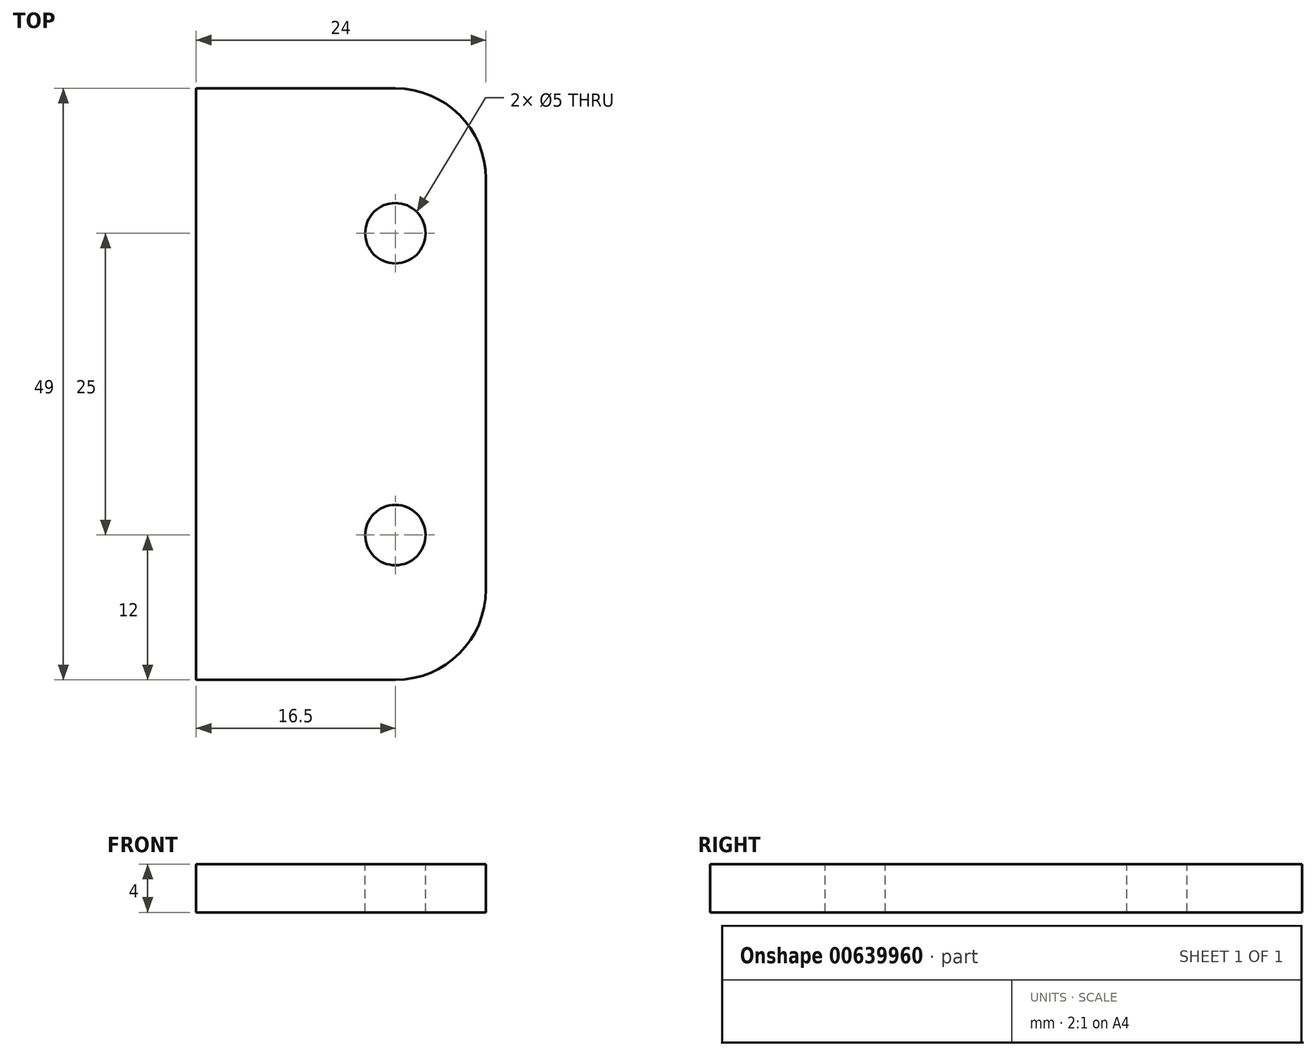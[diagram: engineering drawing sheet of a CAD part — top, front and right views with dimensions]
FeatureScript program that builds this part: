
annotation { "Feature Type Name" : "Feature", "Feature Type Description" : "" }
export const myFeature = defineFeature(function(context is Context, id is Id, definition is map)
    precondition{}
    {
        {
            var Q0;
            Q0=qCreatedBy(makeId("Top.planeOp"),FACE);
            var sketch = newSketch(context, id + "F0", { "sketchPlane" : qUnion([Q0])});
            skLineSegment(sketch, "E0.bottom", {"start": v(12, 24.5) * mm, "end": v(-12, 24.5) * mm});
            skLineSegment(sketch, "E0.top", {"start": v(12, -24.5) * mm, "end": v(-12, -24.5) * mm});
            skLineSegment(sketch, "E0.left", {"start": v(12, 24.5) * mm, "end": v(12, -24.5) * mm});
            skLineSegment(sketch, "E0.right", {"start": v(-12, 24.5) * mm, "end": v(-12, -24.5) * mm});
            skPoint(sketch, "E0.middle", {"position": v(0, 0) * mm});
            skSolve(sketch);
        }
        {
            var Q0;
            Q0=makeQuery(id+"F0.imprint","IMPRINT",FACE,{"disambiguationData":[TD([[makeQuery(id+"F0.imprint","IMPRINT",EDGE,{"derivedFrom":sQuery(id+"F0.wireOp",EDGE,"E0.bottom")}),1.0]])]});
            extrude(context, id + "F1", {"entities" : qUnion([Q0]), "depth" : 4 * mm, "offsetDistance" : 25 * mm});
        }
        {
            var Q0;
            Q0=makeQuery(id+"F1.opExtrude","SWEPT_EDGE",EDGE,{"disambiguationData":[OSD([sQuery(id+"F0.wireOp",EDGE,"E0.top"),sQuery(id+"F0.wireOp",EDGE,"E0.left")])]});
            var Q1;
            Q1=makeQuery(id+"F1.opExtrude","SWEPT_EDGE",EDGE,{"disambiguationData":[OSD([sQuery(id+"F0.wireOp",EDGE,"E0.bottom"),sQuery(id+"F0.wireOp",EDGE,"E0.left")])]});
            fillet(context, id + "F2", {"entities" : qUnion([Q0, Q1]), "radius" : 7.5 * mm, "tangentPropagation" : true, "allowEdgeOverflow" : false});
        }
        {
            var Q0;
            Q0=makeQuery(id+"F1.opExtrude","CAP_FACE",FACE,{"disambiguationData":[OSD([sQuery(id+"F0.wireOp",EDGE,"E0.bottom"),sQuery(id+"F0.wireOp",EDGE,"E0.top"),sQuery(id+"F0.wireOp",EDGE,"E0.left"),sQuery(id+"F0.wireOp",EDGE,"E0.right")])],"isStart":false});
            var sketch = newSketch(context, id + "F3", { "sketchPlane" : qUnion([Q0])});
            skCircle(sketch, "E1", {"center": v(4.5, 12.5) * mm, "radius": 2.5 * mm});
            skCircle(sketch, "E2", {"center": v(4.5, -12.5) * mm, "radius": 2.5 * mm});
            skSolve(sketch);
        }
        {
            var Q0;
            Q0=makeQuery(id+"F3.imprint","IMPRINT",FACE,{"disambiguationData":[TD([[makeQuery(id+"F3.imprint","IMPRINT",EDGE,{"derivedFrom":sQuery(id+"F3.wireOp",EDGE,"E1")}),1.0]])]});
            var Q1;
            Q1=makeQuery(id+"F3.imprint","IMPRINT",FACE,{"disambiguationData":[TD([[makeQuery(id+"F3.imprint","IMPRINT",EDGE,{"derivedFrom":sQuery(id+"F3.wireOp",EDGE,"E2")}),1.0]])]});
            extrude(context, id + "F4", {"entities" : qUnion([Q0, Q1]), "operationType" : NewBodyOperationType.REMOVE, "oppositeDirection" : true, "depth" : 5 * mm, "offsetDistance" : 25 * mm});
        }
    });
